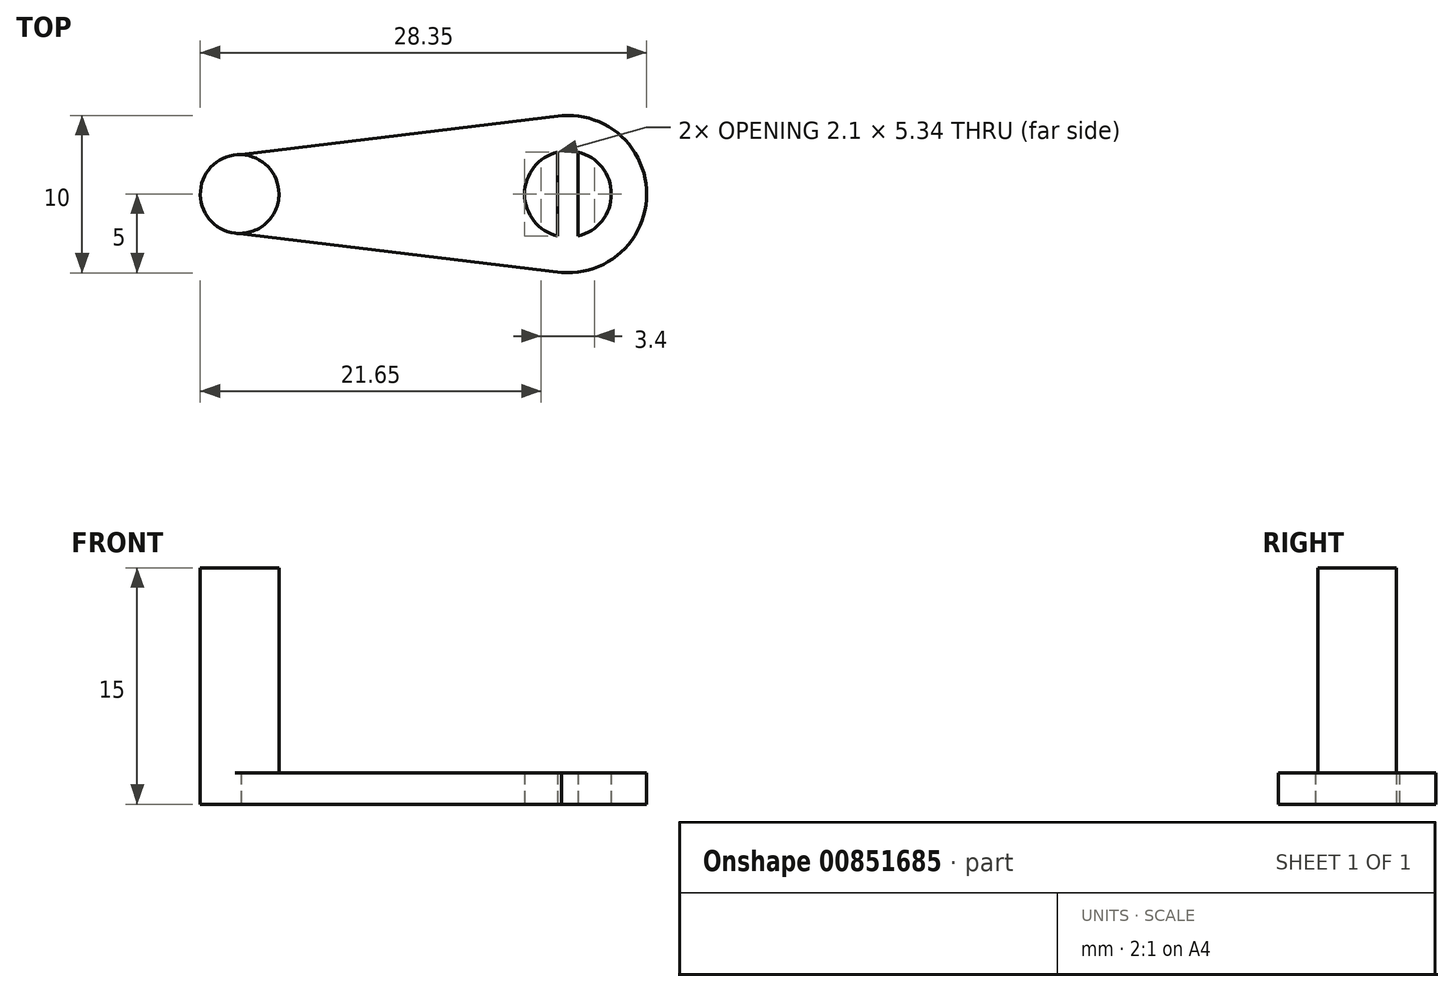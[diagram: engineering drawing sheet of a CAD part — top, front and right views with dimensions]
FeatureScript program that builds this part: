
annotation { "Feature Type Name" : "Feature", "Feature Type Description" : "" }
export const myFeature = defineFeature(function(context is Context, id is Id, definition is map)
    precondition{}
    {
        {
            var Q0;
            Q0=qCreatedBy(makeId("Top.planeOp"),FACE);
            var sketch = newSketch(context, id + "F0", { "sketchPlane" : qUnion([Q0])});
            skCircle(sketch, "E0", {"center": v(0, 0) * mm, "radius": 2.75 * mm});
            skArc(sketch, "E1", {"start": v(-0.8, -4.94) * mm, "mid": v(5, 0.02) * mm, "end": v(-0.84, 4.93) * mm});
            skLineSegment(sketch, "E2.left", {"start": v(0.65, -2.67) * mm, "end": v(0.65, 2.67) * mm});
            skLineSegment(sketch, "E2.right", {"start": v(-0.65, -2.67) * mm, "end": v(-0.65, 2.67) * mm});
            skCircle(sketch, "E3", {"center": v(-20.85, 0) * mm, "radius": 2.5 * mm});
            skLineSegment(sketch, "E4", {"start": v(-0.37, 4.99) * mm, "end": v(-20.77, 2.5) * mm});
            skLineSegment(sketch, "E5", {"start": v(-0.4, -4.98) * mm, "end": v(-21.15, -2.48) * mm});
            skPoint(sketch, "E6.orphan", {"position": v(0.65, 3.03) * mm});
            skPoint(sketch, "E7.orphan", {"position": v(-0.65, 3.03) * mm});
            skPoint(sketch, "E2.bottom.start.orphan", {"position": v(0.65, -3.03) * mm});
            skPoint(sketch, "E8.orphan", {"position": v(-0.65, -3.03) * mm});
            skSolve(sketch);
        }
        {
            var Q0;
            {var subQ0=sQuery(id+"F0.wireOp",EDGE,"E3");var subQ1=makeQuery(id+"F0.imprint","INTERSECT",VERTEX,{"derivedFrom":[subQ0,sQuery(id+"F0.wireOp",EDGE,"E4")]});Q0=makeQuery(id+"F0.imprint","IMPRINT",FACE,{"disambiguationData":[TD([[makeQuery(id+"F0.imprint","IMPRINT",EDGE,{"disambiguationData":[TD([[subQ1,-1.0]])],"derivedFrom":subQ0}),1.0]])]});}
            extrude(context, id + "F1", {"entities" : qUnion([Q0]), "depth" : 15 * mm, "offsetDistance" : 25 * mm});
        }
        {
            var Q0;
            {var subQ0=sQuery(id+"F0.wireOp",EDGE,"E2.left");var subQ1=sQuery(id+"F0.wireOp",EDGE,"E0");var subQ3=makeQuery(id+"F0.imprint","INTERSECT",VERTEX,{"disambiguationData":[OD(1.0)],"derivedFrom":[subQ1,subQ0]});Q0=makeQuery(id+"F0.imprint","IMPRINT",FACE,{"disambiguationData":[TD([[makeQuery(id+"F0.imprint","IMPRINT",EDGE,{"disambiguationData":[TD([[subQ3,-1.0]])],"derivedFrom":subQ1}),-1.0]])]});}
            var Q1;
            {var subQ0=sQuery(id+"F0.wireOp",EDGE,"E2.left");Q1=makeQuery(id+"F0.imprint","IMPRINT",FACE,{"disambiguationData":[TD([[makeQuery(id+"F0.imprint","IMPRINT",EDGE,{"derivedFrom":subQ0}),1.0]])]});}
            extrude(context, id + "F2", {"entities" : qUnion([Q0, Q1]), "operationType" : NewBodyOperationType.ADD, "depth" : 2 * mm, "offsetDistance" : 25 * mm});
        }
    });
